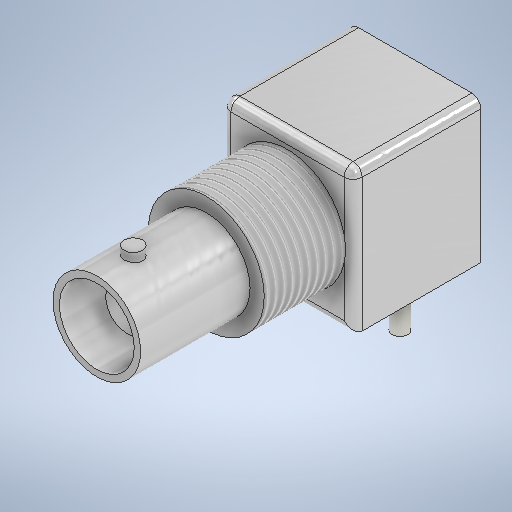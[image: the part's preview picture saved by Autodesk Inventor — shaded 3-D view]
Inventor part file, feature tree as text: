
AUTODESK INVENTOR PART (.ipt)
format: ipt  version: 2025 (Build 290162000, 162)  size: 428,032 bytes
history: native  units: in
note: dims shown in document units (in); Inventor stores cm internally (conversion verified against a paired STEP export)
features: sketch x9, extrude x6, plane x2, thread x1, fillet x1, revolve x1, sweep x1
ambient origin geometry x8: Origin, YZ Plane, XZ Plane, XY Plane, X Axis, Y Axis, Z Axis, Center Point
bodies: Body1 (feature_tree), Body2 (feature_tree)
feature tree (21):
  extrude  "Extrusion3"  Depth=0.5669in
  extrude  "Extrusion4"  Depth=0.5in
  thread  "Thread1"  [1 undecoded]
  fillet  "Fillet1"  Radius=0.3504in
  extrude  "Extrusion5"  Depth=0.378in
  plane  "Work Plane2"
  revolve  "Revolution1"  [1 undecoded]
  extrude  "Extrusion6"  Depth=0.0354in
  extrude  "Extrusion7"  TaperAngle=90.0deg  [1 undecoded]
  extrude  "Extrusion8"  Depth=0.3417in TaperAngle=0.0deg
  sketch  "Sketch12"  dims[d28=0.0681in d29=0.2854in]
  plane  "Work Plane3"
  sweep  "Sweep2"
  sketch  "Sketch5"  dims[d7=0.5669in d8=0.6142in]
  sketch  "Sketch6"  dims[d9=0.5512in d10=0.0in d11=0.5in d12=0.3504in d13=0.0in d14=0.3504in d15=0.0in]
  sketch  "Sketch7"  dims[d16=0.0394in d17=0.378in]
  sketch  "Sketch8"  dims[d18=0.4724in d19=0.0in d20=0.3228in]
  sketch  "Sketch9"  dims[d21=-0.1575in d22=0.0354in]
  sketch  "Sketch10"  dims[d23=0.0394in d24=90.0deg]
  sketch  "Sketch11"  dims[d25=0.185in d26=0.3417in d27=0.0in]
  sketch  "Sketch14"  dims[d30=0.2in d31=0.1614in d32=0.0in d33=0.0551in d34=0.0551in d35=0.0551in d36=0.1339in d37=0.1299in d38=0.1693in d39=0.1693in d40=0.2598in d41=0.2598in d42=0.2559in d43=0.1555in d44=0.1772in d45=0.1772in d46=0.1772in d47=0.0in d48=0.3169in d49=0.0299in d50=0.0283in d51=0.1in d53=0.4854in d54=0.3169in d55=0.0591in d56=0.0in d57=0.0in d4=0.0in d5=0.0in d6=0.0in]
note: 3 required parameter values undecoded (feature->parameter linkage not recoverable at this tier; creation-order binding heuristic only, values carry confidence <= 0.55)